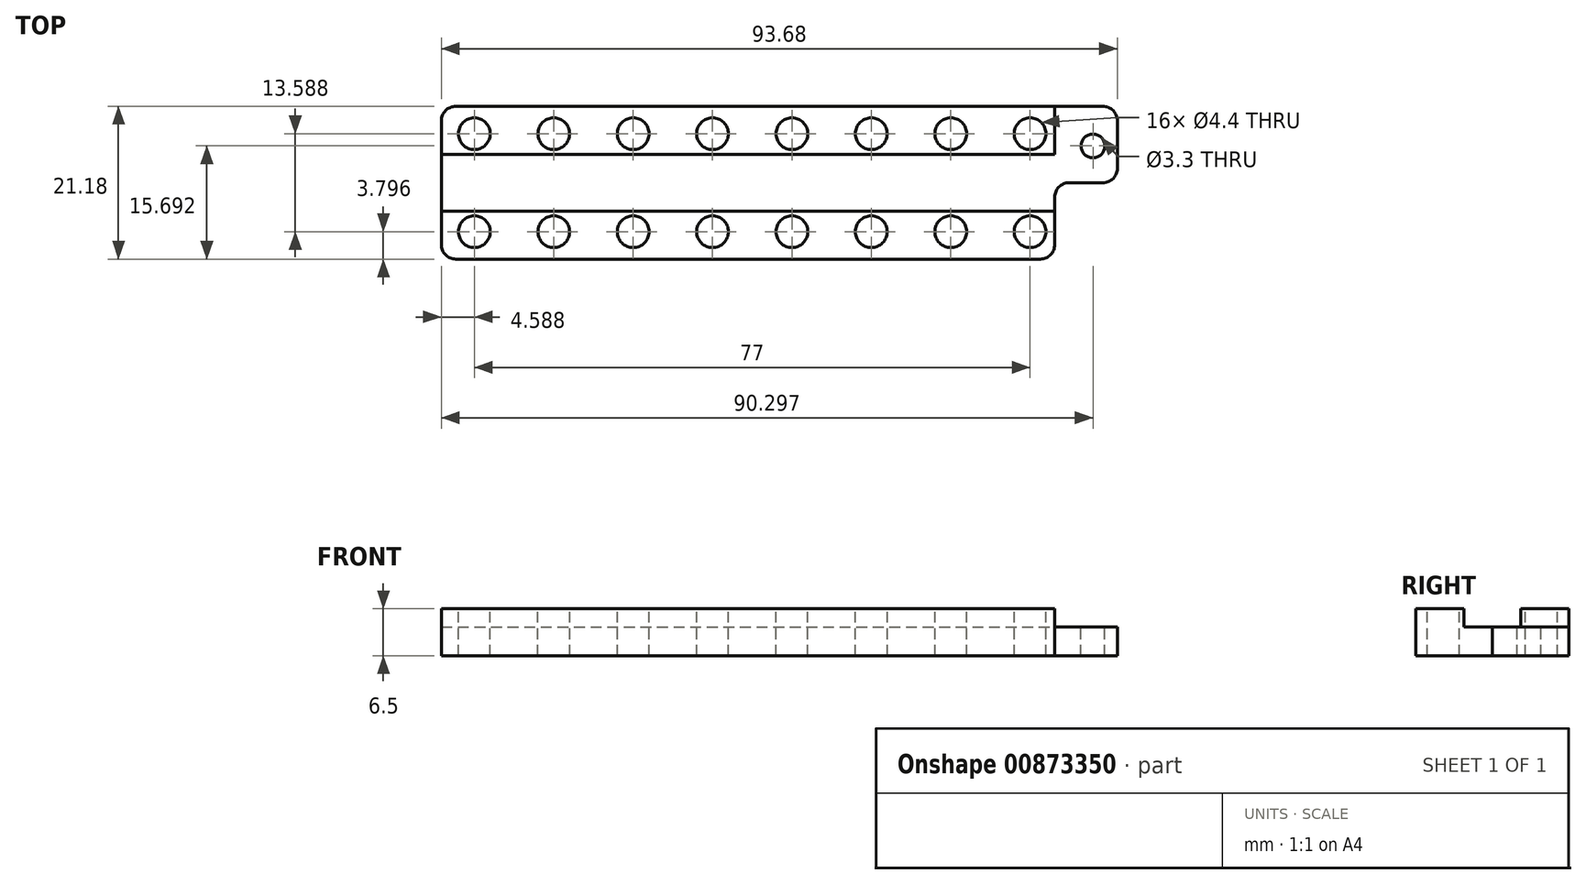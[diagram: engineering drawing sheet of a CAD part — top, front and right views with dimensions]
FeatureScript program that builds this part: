
annotation { "Feature Type Name" : "Feature", "Feature Type Description" : "" }
export const myFeature = defineFeature(function(context is Context, id is Id, definition is map)
    precondition{}
    {
        {
            var Q0;
            Q0=qCreatedBy(makeId("Top.planeOp"),FACE);
            var sketch = newSketch(context, id + "F0", { "sketchPlane" : qUnion([Q0])});
            skLineSegment(sketch, "E0.bottom", {"start": v(42.5, 3.95) * mm, "end": v(-42.5, 3.95) * mm, "construction": true});
            skLineSegment(sketch, "E0.top", {"start": v(42.5, -3.95) * mm, "end": v(-42.5, -3.95) * mm, "construction": true});
            skLineSegment(sketch, "E0.left", {"start": v(42.5, 3.95) * mm, "end": v(42.5, -3.95) * mm, "construction": true});
            skLineSegment(sketch, "E0.right", {"start": v(-42.5, 3.95) * mm, "end": v(-42.5, -3.95) * mm, "construction": true});
            skPoint(sketch, "E0.middle", {"position": v(0, 0) * mm});
            skLineSegment(sketch, "E1.bottom", {"start": v(42.5, 10.59) * mm, "end": v(-42.5, 10.59) * mm});
            skLineSegment(sketch, "E1.top", {"start": v(42.5, -10.59) * mm, "end": v(-42.5, -10.59) * mm});
            skLineSegment(sketch, "E1.left", {"start": v(42.5, 10.59) * mm, "end": v(42.5, -10.59) * mm});
            skLineSegment(sketch, "E1.right", {"start": v(-42.5, 10.59) * mm, "end": v(-42.5, -10.59) * mm});
            skLineSegment(sketch, "E2", {"start": v(-42.5, 3.95) * mm, "end": v(42.5, 3.95) * mm});
            skLineSegment(sketch, "E3", {"start": v(42.5, -3.95) * mm, "end": v(-42.5, -3.95) * mm});
            skSolve(sketch);
        }
        {
            var Q0;
            {var subQ0=sQuery(id+"F0.wireOp",EDGE,"E1.bottom");Q0=makeQuery(id+"F0.imprint","IMPRINT",FACE,{"disambiguationData":[TD([[makeQuery(id+"F0.imprint","IMPRINT",EDGE,{"derivedFrom":subQ0}),1.0]])]});}
            var Q1;
            {var subQ0=sQuery(id+"F0.wireOp",EDGE,"E2");Q1=makeQuery(id+"F0.imprint","IMPRINT",FACE,{"disambiguationData":[TD([[makeQuery(id+"F0.imprint","IMPRINT",EDGE,{"derivedFrom":subQ0}),-1.0]])]});}
            var Q2;
            {var subQ0=sQuery(id+"F0.wireOp",EDGE,"E1.top");Q2=makeQuery(id+"F0.imprint","IMPRINT",FACE,{"disambiguationData":[TD([[makeQuery(id+"F0.imprint","IMPRINT",EDGE,{"derivedFrom":subQ0}),-1.0]])]});}
            extrude(context, id + "F1", {"entities" : qUnion([Q0, Q1, Q2]), "oppositeDirection" : true, "depth" : (4) * mm, "offsetDistance" : 25 * mm});
        }
        {
            var Q0;
            {var subQ0=sQuery(id+"F0.wireOp",EDGE,"E1.bottom");Q0=makeQuery(id+"F0.imprint","IMPRINT",FACE,{"disambiguationData":[TD([[makeQuery(id+"F0.imprint","IMPRINT",EDGE,{"derivedFrom":subQ0}),1.0]])]});}
            var Q1;
            {var subQ0=sQuery(id+"F0.wireOp",EDGE,"E1.top");Q1=makeQuery(id+"F0.imprint","IMPRINT",FACE,{"disambiguationData":[TD([[makeQuery(id+"F0.imprint","IMPRINT",EDGE,{"derivedFrom":subQ0}),-1.0]])]});}
            extrude(context, id + "F2", {"entities" : qUnion([Q0, Q1]), "operationType" : NewBodyOperationType.ADD, "depth" : 2.5 * mm, "offsetDistance" : 25 * mm});
        }
        {
            var Q0;
            Q0=makeQuery(id+"F2.opExtrude","CAP_FACE",FACE,{"disambiguationData":[OSD([sQuery(id+"F0.wireOp",EDGE,"E1.bottom"),sQuery(id+"F0.wireOp",EDGE,"E1.left"),sQuery(id+"F0.wireOp",EDGE,"E1.right"),sQuery(id+"F0.wireOp",EDGE,"E2")])],"isStart":false});
            var sketch = newSketch(context, id + "F3", { "sketchPlane" : qUnion([Q0])});
            skPoint(sketch, "E4", {"position": v(-37.91, 6.8) * mm});
            skPoint(sketch, "E5.1.0.0", {"position": v(-26.91, 6.8) * mm});
            skPoint(sketch, "E5.2.0.0", {"position": v(-15.91, 6.8) * mm});
            skPoint(sketch, "E5.3.0.0", {"position": v(-4.91, 6.8) * mm});
            skPoint(sketch, "E5.4.0.0", {"position": v(6.09, 6.8) * mm});
            skPoint(sketch, "E5.5.0.0", {"position": v(17.09, 6.8) * mm});
            skPoint(sketch, "E5.6.0.0", {"position": v(28.09, 6.8) * mm});
            skPoint(sketch, "E5.7.0.0", {"position": v(39.09, 6.8) * mm});
            skLineSegment(sketch, "E5.direction1", {"start": v(-37.91, 6.8) * mm, "end": v(-26.91, 6.8) * mm, "construction": true});
            skPoint(sketch, "E6.MirrorP", {"position": v(-37.91, -6.8) * mm});
            skPoint(sketch, "E7.MirrorP", {"position": v(-15.91, -6.8) * mm});
            skPoint(sketch, "E8.MirrorP", {"position": v(28.09, -6.8) * mm});
            skPoint(sketch, "E9.MirrorP", {"position": v(6.09, -6.8) * mm});
            skLineSegment(sketch, "E10.MirrorCS", {"start": v(-37.91, -6.8) * mm, "end": v(-26.91, -6.8) * mm, "construction": true});
            skPoint(sketch, "E11.MirrorP", {"position": v(39.09, -6.8) * mm});
            skPoint(sketch, "E12.MirrorP", {"position": v(-26.91, -6.8) * mm});
            skPoint(sketch, "E13.MirrorP", {"position": v(17.09, -6.8) * mm});
            skPoint(sketch, "E14.MirrorP", {"position": v(-4.91, -6.8) * mm});
            skSolve(sketch);
        }
        {
            var Q0;
            Q0=sQuery(id+"F3.wireOp",VERTEX,"E4");
            var Q1;
            Q1=sQuery(id+"F3.wireOp",VERTEX,"E6.MirrorP");
            var Q2;
            Q2=sQuery(id+"F3.wireOp",VERTEX,"E5.1.0.0");
            var Q3;
            Q3=sQuery(id+"F3.wireOp",VERTEX,"E12.MirrorP");
            var Q4;
            Q4=sQuery(id+"F3.wireOp",VERTEX,"E5.2.0.0");
            var Q5;
            Q5=sQuery(id+"F3.wireOp",VERTEX,"E7.MirrorP");
            var Q6;
            Q6=sQuery(id+"F3.wireOp",VERTEX,"E5.3.0.0");
            var Q7;
            Q7=sQuery(id+"F3.wireOp",VERTEX,"E14.MirrorP");
            var Q8;
            Q8=sQuery(id+"F3.wireOp",VERTEX,"E5.4.0.0");
            var Q9;
            Q9=sQuery(id+"F3.wireOp",VERTEX,"E9.MirrorP");
            var Q10;
            Q10=sQuery(id+"F3.wireOp",VERTEX,"E13.MirrorP");
            var Q11;
            Q11=sQuery(id+"F3.wireOp",VERTEX,"E5.5.0.0");
            var Q12;
            Q12=sQuery(id+"F3.wireOp",VERTEX,"E5.6.0.0");
            var Q13;
            Q13=sQuery(id+"F3.wireOp",VERTEX,"E8.MirrorP");
            var Q14;
            Q14=sQuery(id+"F3.wireOp",VERTEX,"E11.MirrorP");
            var Q15;
            Q15=sQuery(id+"F3.wireOp",VERTEX,"E5.7.0.0");
            var Q16;
            Q16=makeQuery(id+"F1.opExtrude","SWEPT_BODY",BODY,{"disambiguationData":[OSD([sQuery(id+"F0.wireOp",EDGE,"E1.bottom"),sQuery(id+"F0.wireOp",EDGE,"E1.top"),sQuery(id+"F0.wireOp",EDGE,"E1.left"),sQuery(id+"F0.wireOp",EDGE,"E1.right")])]});
            hole(context, id + "F4", {"style" : HoleStyle.SIMPLE, "endStyle" : HoleEndStyle.BLIND, "standardTappedOrClearance" : lookupTablePath({ "fit" : "Normal", "standard" : "ISO", "size" : "M4", "type" : "Clearance" }), "standardBlindInLast" : lookupTablePath({ "fit" : "Standard", "standard" : "ISO", "size" : "M4", "type" : "Clearance" }), "holeDiameter" : 4.4 * mm, "majorDiameter" : 5 * mm, "holeDepth" : 25 * mm, "isTappedThrough" : true, "tappedDepth" : 12 * mm, "tapClearance" : 3, "startFromSketch" : true, "locations" : qUnion([Q0, Q1, Q2, Q3, Q4, Q5, Q6, Q7, Q8, Q9, Q10, Q11, Q12, Q13, Q14, Q15]), "scope" : qUnion([Q16])});
        }
        {
            var Q0;
            Q0=qCreatedBy(makeId("Top.planeOp"),FACE);
            var sketch = newSketch(context, id + "F5", { "sketchPlane" : qUnion([Q0])});
            skLineSegment(sketch, "E15", {"start": v(42.46, 10.59) * mm, "end": v(51.18, 10.59) * mm});
            skLineSegment(sketch, "E16", {"start": v(51.18, 10.59) * mm, "end": v(51.18, 0) * mm});
            skLineSegment(sketch, "E17", {"start": v(51.18, 0) * mm, "end": v(42.5, 0) * mm});
            skLineSegment(sketch, "E18", {"start": v(42.5, 0) * mm, "end": v(42.46, 10.59) * mm});
            skPoint(sketch, "E19", {"position": v(47.8, 5.1) * mm});
            skSolve(sketch);
        }
        {
            var Q0;
            Q0=makeQuery(id+"F5.imprint","IMPRINT",FACE,{"disambiguationData":[TD([[makeQuery(id+"F5.imprint","IMPRINT",EDGE,{"derivedFrom":sQuery(id+"F5.wireOp",EDGE,"E15")}),-1.0]])]});
            extrude(context, id + "F6", {"entities" : qUnion([Q0]), "operationType" : NewBodyOperationType.ADD, "oppositeDirection" : true, "depth" : 4 * mm, "offsetDistance" : 25 * mm});
        }
        {
            var Q0;
            Q0=sQuery(id+"F5.wireOp",VERTEX,"E19");
            var Q1;
            Q1=makeQuery(id+"F1.opExtrude","SWEPT_BODY",BODY,{"disambiguationData":[OSD([sQuery(id+"F0.wireOp",EDGE,"E1.bottom"),sQuery(id+"F0.wireOp",EDGE,"E1.top"),sQuery(id+"F0.wireOp",EDGE,"E1.left"),sQuery(id+"F0.wireOp",EDGE,"E1.right")])]});
            hole(context, id + "F7", {"style" : HoleStyle.SIMPLE, "endStyle" : HoleEndStyle.BLIND, "standardTappedOrClearance" : lookupTablePath({ "fit" : "Normal", "standard" : "ISO", "size" : "M3", "type" : "Clearance" }), "standardBlindInLast" : lookupTablePath({ "fit" : "Standard", "standard" : "ISO", "size" : "M3", "type" : "Clearance" }), "holeDiameter" : 3.3 * mm, "majorDiameter" : 5 * mm, "holeDepth" : 25 * mm, "isTappedThrough" : true, "tappedDepth" : 12 * mm, "tapClearance" : 3, "startFromSketch" : true, "locations" : qUnion([Q0]), "scope" : qUnion([Q1])});
        }
        {
            var Q0;
            {var subQ0=sQuery(id+"F0.wireOp",EDGE,"E1.right");var subQ1=sQuery(id+"F0.wireOp",EDGE,"E1.bottom");Q0=makeQuery(id+"F2.boolean.opBoolean","MERGE",EDGE,{"derivedFrom":[makeQuery(id+"F1.opExtrude","SWEPT_EDGE",EDGE,{"disambiguationData":[OSD([subQ1,subQ0])]}),makeQuery(id+"F2.opExtrude","SWEPT_EDGE",EDGE,{"disambiguationData":[OSD([subQ1,subQ0])]})]});}
            var Q1;
            {var subQ0=sQuery(id+"F0.wireOp",EDGE,"E1.right");var subQ1=sQuery(id+"F0.wireOp",EDGE,"E1.top");Q1=makeQuery(id+"F2.boolean.opBoolean","MERGE",EDGE,{"derivedFrom":[makeQuery(id+"F1.opExtrude","SWEPT_EDGE",EDGE,{"disambiguationData":[OSD([subQ1,subQ0])]}),makeQuery(id+"F2.opExtrude","SWEPT_EDGE",EDGE,{"disambiguationData":[OSD([subQ1,subQ0])]})]});}
            var Q2;
            Q2=makeQuery(id+"F6.opExtrude","SWEPT_EDGE",EDGE,{"disambiguationData":[OSD([sQuery(id+"F5.wireOp",EDGE,"E15"),sQuery(id+"F5.wireOp",EDGE,"E16")])]});
            var Q3;
            Q3=makeQuery(id+"F6.opExtrude","SWEPT_EDGE",EDGE,{"disambiguationData":[OSD([sQuery(id+"F5.wireOp",EDGE,"E16"),sQuery(id+"F5.wireOp",EDGE,"E17")])]});
            var Q4;
            {var subQ0=sQuery(id+"F0.wireOp",EDGE,"E1.left");var subQ1=sQuery(id+"F0.wireOp",EDGE,"E1.top");Q4=makeQuery(id+"F2.boolean.opBoolean","MERGE",EDGE,{"derivedFrom":[makeQuery(id+"F1.opExtrude","SWEPT_EDGE",EDGE,{"disambiguationData":[OSD([subQ1,subQ0])]}),makeQuery(id+"F2.opExtrude","SWEPT_EDGE",EDGE,{"disambiguationData":[OSD([subQ1,subQ0])]})]});}
            var Q5;
            Q5=makeQuery(id+"F6.opExtrude","SWEPT_EDGE",EDGE,{"disambiguationData":[OSD([sQuery(id+"F5.wireOp",EDGE,"E17"),sQuery(id+"F5.wireOp",EDGE,"E18")])]});
            fillet(context, id + "F8", {"entities" : qUnion([Q0, Q1, Q2, Q3, Q4, Q5]), "radius" : 2 * mm, "tangentPropagation" : true, "allowEdgeOverflow" : false});
        }
    });
